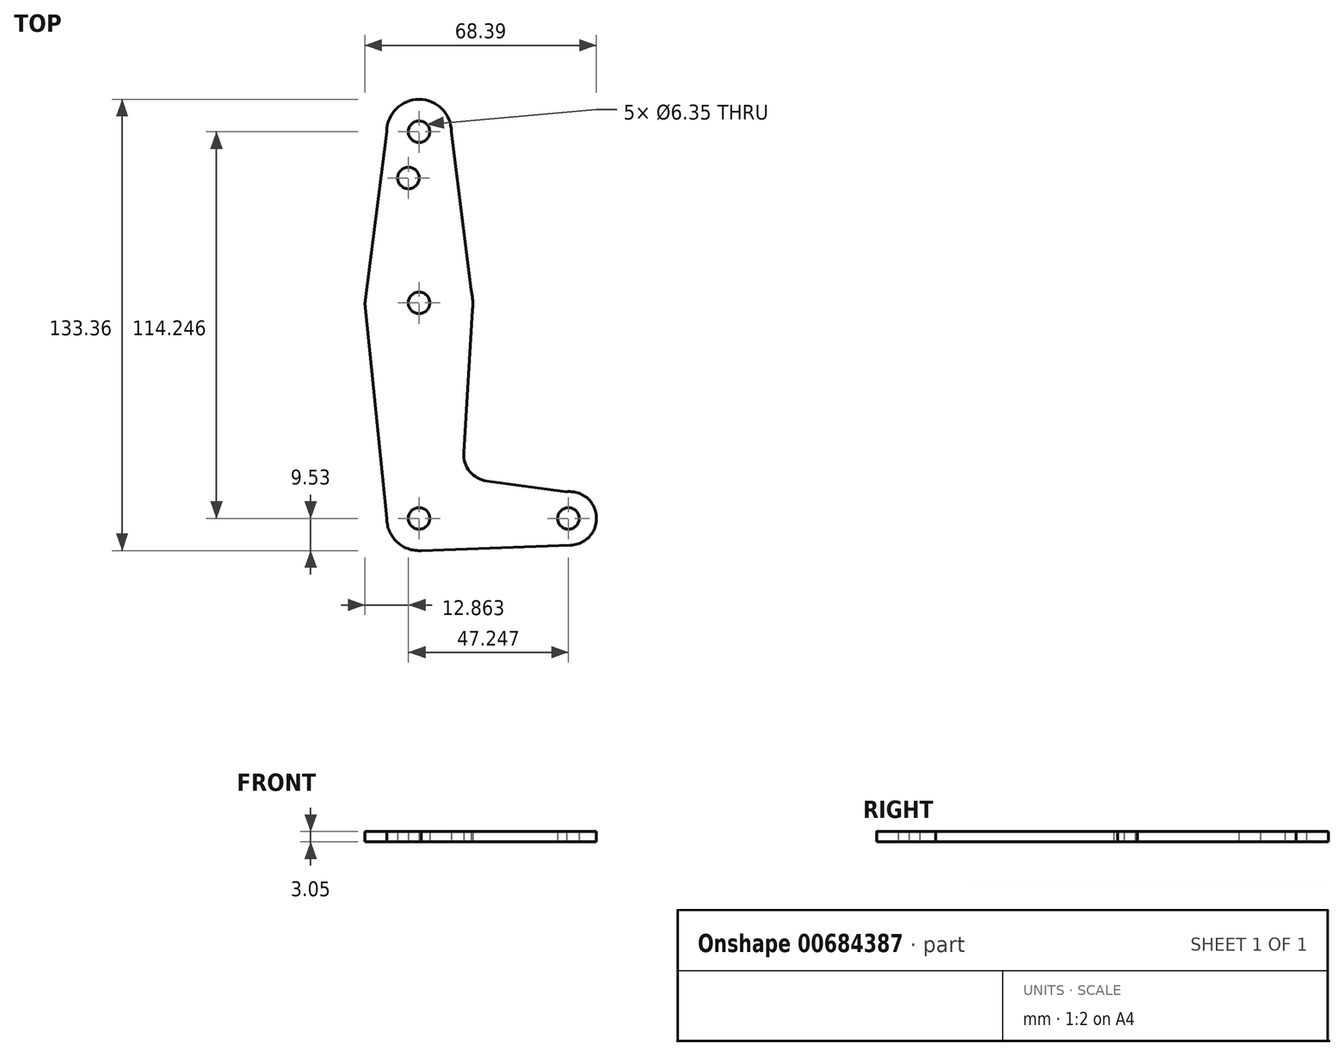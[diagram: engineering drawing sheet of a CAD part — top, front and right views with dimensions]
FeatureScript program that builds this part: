
annotation { "Feature Type Name" : "Feature", "Feature Type Description" : "" }
export const myFeature = defineFeature(function(context is Context, id is Id, definition is map)
    precondition{}
    {
        {
            var Q0;
            Q0=qCreatedBy(makeId("Top.planeOp"),FACE);
            var sketch = newSketch(context, id + "F0", { "sketchPlane" : qUnion([Q0])});
            skCircle(sketch, "E0", {"center": v(0, 114.3) * mm, "radius": 9.53 * mm});
            skCircle(sketch, "E1", {"center": v(44.45, 0) * mm, "radius": 7.94 * mm});
            skCircle(sketch, "E2", {"center": v(0, 63.5) * mm, "radius": 15.88 * mm});
            skLineSegment(sketch, "E3", {"start": v(0, 100.03) * mm, "end": v(-3.18, 100.03) * mm});
            skLineSegment(sketch, "E4", {"start": v(9.53, 114.3) * mm, "end": v(15.88, 63.5) * mm});
            skLineSegment(sketch, "E5", {"start": v(-9.53, 114.3) * mm, "end": v(-16, 63.5) * mm});
            skCircle(sketch, "E6", {"center": v(0, 0) * mm, "radius": 9.53 * mm});
            skLineSegment(sketch, "E7", {"start": v(0, -9.53) * mm, "end": v(44.73, -7.93) * mm});
            skLineSegment(sketch, "E8", {"start": v(43.54, 7.89) * mm, "end": v(20.07, 11.02) * mm});
            skLineSegment(sketch, "E9", {"start": v(13.18, 19.39) * mm, "end": v(15.88, 63.5) * mm});
            skPoint(sketch, "E10.visualSharp", {"position": v(12.73, 12) * mm});
            skArc(sketch, "E10.filletArc", {"start": v(13.18, 19.39) * mm, "mid": v(14.98, 13.85) * mm, "end": v(20.07, 11.02) * mm});
            skLineSegment(sketch, "E11", {"start": v(-16, 63.5) * mm, "end": v(-9.52, 0) * mm});
            skSolve(sketch);
        }
        {
            var Q0;
            Q0=qCreatedBy(makeId("Top.planeOp"),FACE);
            var sketch = newSketch(context, id + "F1", { "sketchPlane" : qUnion([Q0])});
            skCircle(sketch, "E12", {"center": v(0, 114.25) * mm, "radius": 3.18 * mm});
            skCircle(sketch, "E13", {"center": v(-3.14, 100.59) * mm, "radius": 3.18 * mm});
            skCircle(sketch, "E14", {"center": v(0, 63.68) * mm, "radius": 3.18 * mm});
            skCircle(sketch, "E15", {"center": v(44.1, 0) * mm, "radius": 3.18 * mm});
            skCircle(sketch, "E16", {"center": v(0, 0) * mm, "radius": 3.18 * mm});
            skSolve(sketch);
        }
        {
            var Q0;
            Q0 = qSketchRegion(id + "F0", true);
            extrude(context, id + "F2", {"entities" : qUnion([Q0]), "depth" : 3.05 * mm, "offsetDistance" : 25.4 * mm});
        }
        {
            var Q0;
            Q0 = qSketchRegion(id + "F1", true);
            extrude(context, id + "F3", {"entities" : qUnion([Q0]), "operationType" : NewBodyOperationType.REMOVE, "depth" : 25.4 * mm, "offsetDistance" : 25.4 * mm});
        }
    });
